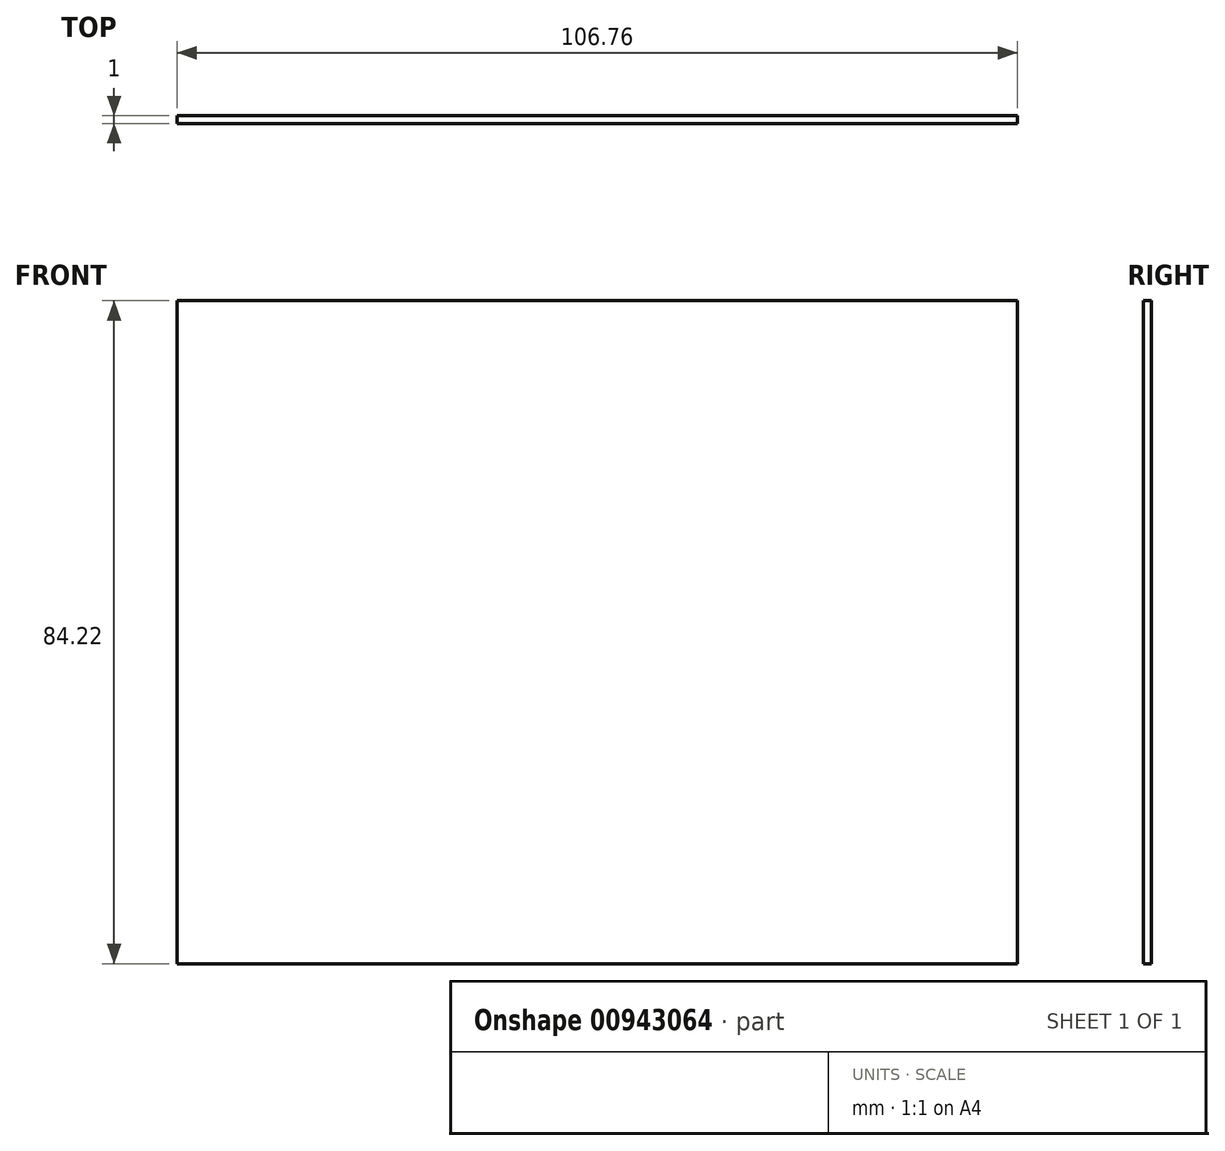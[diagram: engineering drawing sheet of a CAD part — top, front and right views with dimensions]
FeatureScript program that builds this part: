
annotation { "Feature Type Name" : "Feature", "Feature Type Description" : "" }
export const myFeature = defineFeature(function(context is Context, id is Id, definition is map)
    precondition{}
    {
        {
            var Q0;
            Q0=qCreatedBy(makeId("Front.planeOp"),FACE);
            var sketch = newSketch(context, id + "F0", { "sketchPlane" : qUnion([Q0])});
            skLineSegment(sketch, "E0.bottom", {"start": v(-52.74, 50.9) * mm, "end": v(54.02, 50.9) * mm});
            skLineSegment(sketch, "E0.top", {"start": v(-52.74, -33.32) * mm, "end": v(54.02, -33.32) * mm});
            skLineSegment(sketch, "E0.left", {"start": v(-52.74, 50.9) * mm, "end": v(-52.74, -33.32) * mm});
            skLineSegment(sketch, "E0.right", {"start": v(54.02, 50.9) * mm, "end": v(54.02, -33.32) * mm});
            skSolve(sketch);
        }
        {
            var Q0;
            Q0=makeQuery(id+"F0.imprint","IMPRINT",FACE,{"disambiguationData":[TD([[makeQuery(id+"F0.imprint","IMPRINT",EDGE,{"derivedFrom":sQuery(id+"F0.wireOp",EDGE,"E0.bottom")}),-1.0]])]});
            extrude(context, id + "F1", {"entities" : qUnion([Q0]), "depth" : 1 * mm, "offsetDistance" : 25 * mm});
        }
    });
